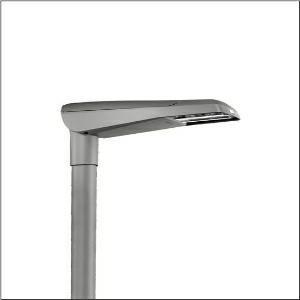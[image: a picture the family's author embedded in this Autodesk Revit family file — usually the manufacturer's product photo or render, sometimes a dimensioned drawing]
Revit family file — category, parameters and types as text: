
# Revit family: streetlight_sl_11_iq_micro___st1_0ab_5xc1nc1f08ce_393e
name_source: partatom
category: Lighting Fixtures
units: mm (PartAtom-declared; Revit-internal decimal feet)

## family parameters
Cut with Voids When Loaded = No
Host = Face
Light Source = No
Part Type = Normal
Room Calculation Point = No
Round Connector Dimension = Use Diameter
Shared = No

## types (1)
- --- (1 x LED, 1280 lm, 14 W, 2200K)
    Apparent Load = 14 VA
    CIE Flux Codes = 29 63 95 100 100
    Color Rendering = 70
    Color Temperature = 2200K
    Default Elevation = 1800 mm
    Description = Streetlight SL 11 iQ micro, mast luminaire, primary light control with 3 zone facetted reflector, of plastic, silver coated, highly specular, primary optical cover: cover, of PMMA, transparent, light distribution: ST1.0aB, light emission: direct distribution, primary light characteristic: asymmetric, installation type: post-top, side-entry, lamps: LED, High Power LED, rated values: 1.500lm | 13,8W | 108,7lm/W (begin service life); end service life: 1.500lm | 14W; at 50% lumin. flux: 750lm | 7,5W | 100lm/W, colour temperature: 2200/2700/3000/4000K, colour rendering: CRI > 70, light colour: 722/727/730/740, light setting 1 begin service life: 100% | 1.500lm | 13,8W | 108,7lm/W | 3.000K, light setting 1 end service life: 14W, further light settings possible, control: Street-Remote, Auto-Match, Temp-Guard, Lumen-Switch, Night-Set, Smart-Wire, Light-Fading, Desk-Remote (wireless, voltage-free reading and setting of iQ features in the workshop via application-optimized NFC function/RFID function), optimised constant luminous flux control (CLO 2.0), with cable H07RN-F 5x 1.5mm², mains connection: 220..240V, AC, 50/60Hz, connection cable pre-assembled, cable length: 5,5m, luminaire housing, of diecast aluminium, powder-coated, Siteco® metallic grey (DB 702S), please order mast flange separately, inclination adjustable without tools: 0°, 5°, 10°, 15° (post-top) | 0°, -5°, -10°, -15° (side-entry), sealing non-destructively replaceable, multi-level sealing system, length: 600mm, width: 174mm, height: 116mm, mast flange for spigot size: 42mm (side-entry): 5XC10008XM4, 60/48mm (side-entry/post-top): 5XC10108XM2, 76/60mm (side-entry/post-top): 5XC10108XM1, equipment: standard, protection rating (complete): IP66, insulation class (complete): insulation class II (safety insulation), certification: CE, ENEC, ENEC+, VDE, impact resistance: IK10, permissible operating ambient temperature for outdoor applications: -25..+50°C, standard-compliant lighting for roads and squares, Environmental Product Declaration (EPD) tested and certified by an independent institute, packaging unit: 1 piece

Light Distribution: ST1.0aB
    Height = 116 mm
    Lamp = 1 x LED
    Lamp Light Flux = 1280 lm
    Lamp Power = 14 W
    Lamp count = 1
    Length = 600 mm
    Luminous efficacy = 91 lm/W
    Manufacturer = Siteco
    ModVariant = No
    Model = 5XC1NC1F08CE
    Number of Poles = 1
    OnlyDefault = Yes
    Power Factor = 1
    Product Name = Streetlight SL 11 iQ micro | ST1.0aB
    Product group = mast luminaire | pylon top
    ProductGroupID = 6100
    Protection Class = Protection class II
    Protection Degree = IP 66
    RLX_Detail_Level = 1
    RLX_Emergency_Light_Flux = 0 lm
    RLX_Emergency_Type = 0
    RLX_Emergency_Type_DB = No
    RlxData = <blob elided: 57997 chars, md5=8f667c1b>
    Socket = socket
    Standby Power = 0 W
    System Light Flux = 1280 lm
    System Power = 14 W
    Type Comments = individual setting: luminous flux: 100 % | dim-lin: 254 | 369 mA
    Type Image = l_1006566.jpg
    URL = http://relux.com
    VarID = @adj_020329
    Voltage = 0 V
    Weight = 0.00 kg
    Width = 174 mm

## geometry (parser evidence)
native form markers: Blend x4, Sweep x11
no freeform markers — native parametric forms only
